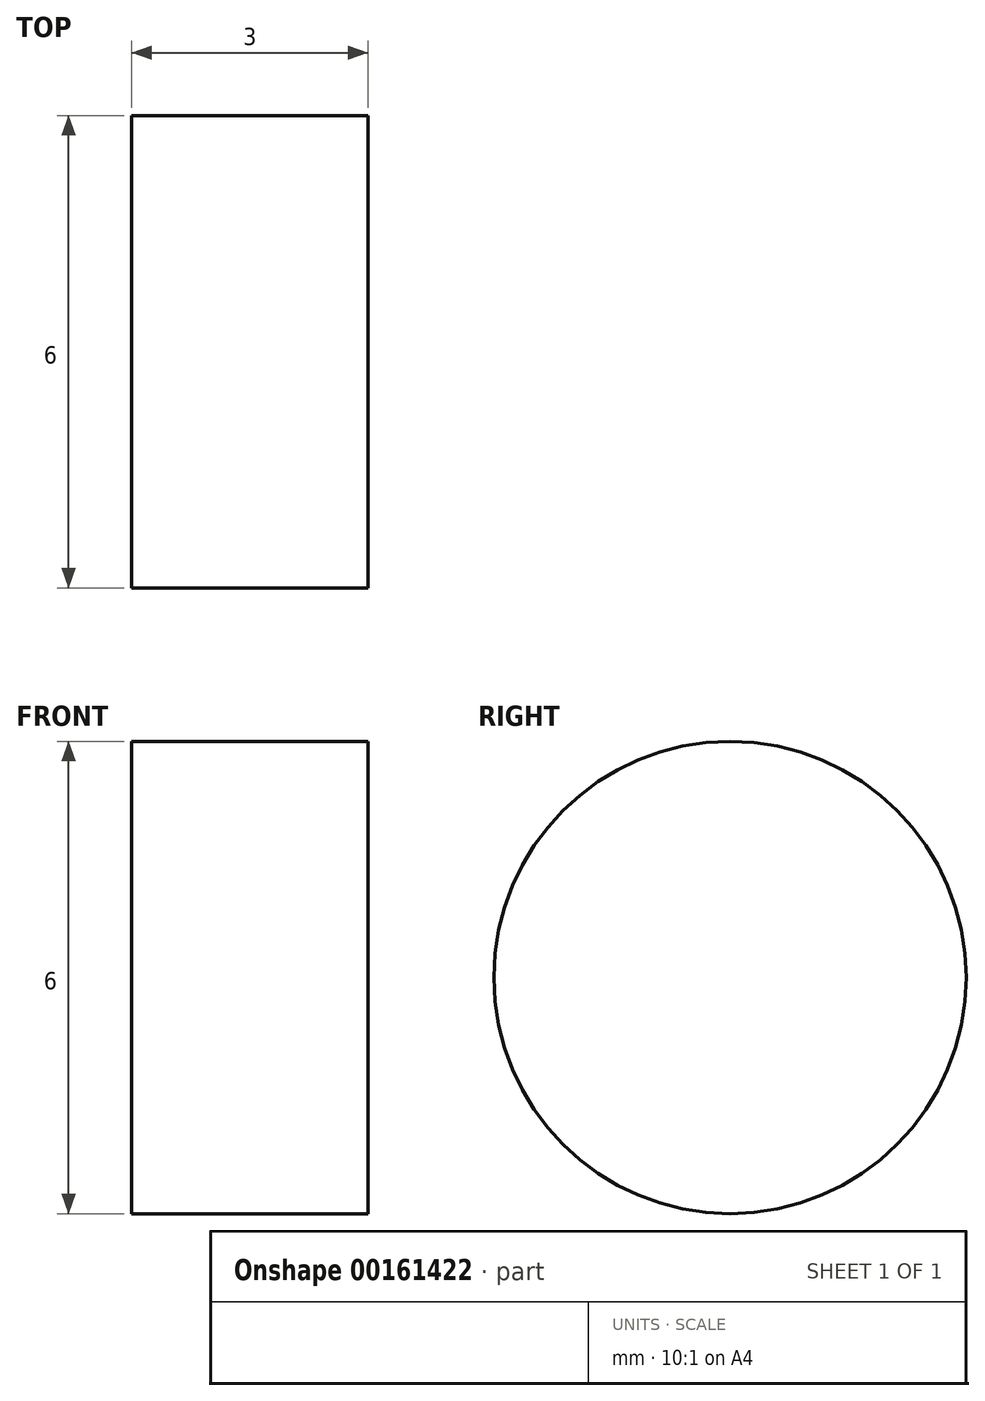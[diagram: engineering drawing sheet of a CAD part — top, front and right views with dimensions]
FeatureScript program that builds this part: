
annotation { "Feature Type Name" : "Feature", "Feature Type Description" : "" }
export const myFeature = defineFeature(function(context is Context, id is Id, definition is map)
    precondition{}
    {
        {
            var Q0;
            Q0=qCreatedBy(makeId("Right.planeOp"),FACE);
            var sketch = newSketch(context, id + "F0", { "sketchPlane" : qUnion([Q0])});
            skCircle(sketch, "E0", {"center": v(0, 0) * mm, "radius": 3 * mm});
            skSolve(sketch);
        }
        {
            var Q0;
            Q0=qSketchRegion(id+"F0",true);
            extrude(context, id + "F1", {"entities" : qUnion([Q0]), "depth" : 3 * mm});
        }
    });
